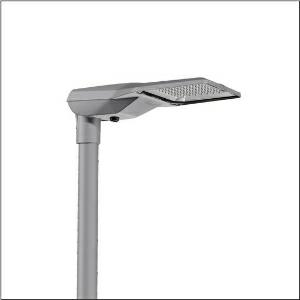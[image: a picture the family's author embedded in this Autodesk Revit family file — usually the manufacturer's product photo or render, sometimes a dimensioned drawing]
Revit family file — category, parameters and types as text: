
# Revit family: streetlight_sl_21_midi___st1_0a_5xe3d33r08lb_2d19
name_source: partatom
category: Lighting Fixtures
units: mm (PartAtom-declared; Revit-internal decimal feet)

## family parameters
Cut with Voids When Loaded = No
Host = Face
Light Source = No
Part Type = Normal
Room Calculation Point = No
Round Connector Dimension = Use Diameter
Shared = No

## types (1)
- --- (1 x LED, 14340 lm, 99.6 W, 3000K)
    Apparent Load = 100 VA
    CIE Flux Codes = 37 72 97 100 100
    Color Rendering = 70
    Color Temperature = 3000K
    Default Elevation = 1800 mm
    Description = Streetlight SL 21 midi, mast luminaire, primary light control with lens, of PMMA, primary optical cover: cover, of toughened safety glass, transparent, light distribution: ST1.0a, light emission: direct distribution, primary light characteristic: asymmetric, installation type: side-entry, post-top, LED, High Power LED, rated luminous flux: 14.340lm, luminous efficacy: 144lm/W, light colour: 730, colour temperature: 3000K, control gear: D4i, control: flexible luminous flux parameterisation, time-dependent luminous flux control, constant luminous flux control, overheat protection, pre-setting: logarithmic dimming characteristic, mains connection: 230..240V, AC, 50/60Hz, start of lifetime: 100W, end of service life: 102W, reduction: 46W, luminaire housing, of diecast aluminium, powder-coated, Siteco® metallic grey (DB 702S), corrosivity category C5 mid according to DIN EN ISO 12944, please order mast flange separately, inclination adjustable: 0°, 5°, 10°, 15°, sealing non-destructively replaceable, multi-level sealing system, length: 644mm, width: 335mm, height: 110mm, mast flange for spigot size: 42mm (side-entry): 5XC10008XM4, 60/48mm (side-entry/post-top): 5XC10108XM2, 76/60mm (side-entry/post-top): 5XC10108XM1, mounting height: 4..8m, Smart Interface below, protection rating (complete): IP66, insulation class (complete): insulation class II (safety insulation), certification: CE, ENEC, ENEC+, VDE, impact resistance: IK10, permissible operating ambient temperature for outdoor applications: -40..+50°C, standard-compliant lighting for roads and squares, packaging unit: 1 piece

Light Distribution: ST1.0a
    Height = 111 mm
    Lamp = 1 x LED
    Lamp Light Flux = 14340 lm
    Lamp Power = 99.6 W
    Lamp count = 1
    Length = 644 mm
    Luminous efficacy = 144 lm/W
    Manufacturer = Siteco
    ModVariant = No
    Model = 5XE3D33R08LB
    Number of Poles = 1
    OnlyDefault = Yes
    Power Factor = 1
    Product Name = Streetlight SL 21 midi | ST1.0a
    Product group = mast luminaire | pylon top
    ProductGroupID = 6100
    Protection Class = Protection class II
    Protection Degree = IP 66
    RLX_Detail_Level = 1
    RLX_Emergency_Light_Flux = 0 lm
    RLX_Emergency_Type = 0
    RLX_Emergency_Type_DB = No
    RlxData = <blob elided: 26953 chars, md5=67c486b7>
    Socket = socket
    Standby Power = 0 W
    System Light Flux = 14340 lm
    System Power = 100 W
    Type Comments = factory setting: luminous flux: 100 % | dim-lin: 254 | 1020 mA
    Type Image = l_1004300.jpg
    URL = http://relux.com
    VarID = @adj_032047
    Voltage = 0 V
    Weight = 0.00 kg
    Width = 336 mm

## geometry (parser evidence)
native form markers: Blend x4, Sweep x11
no freeform markers — native parametric forms only
